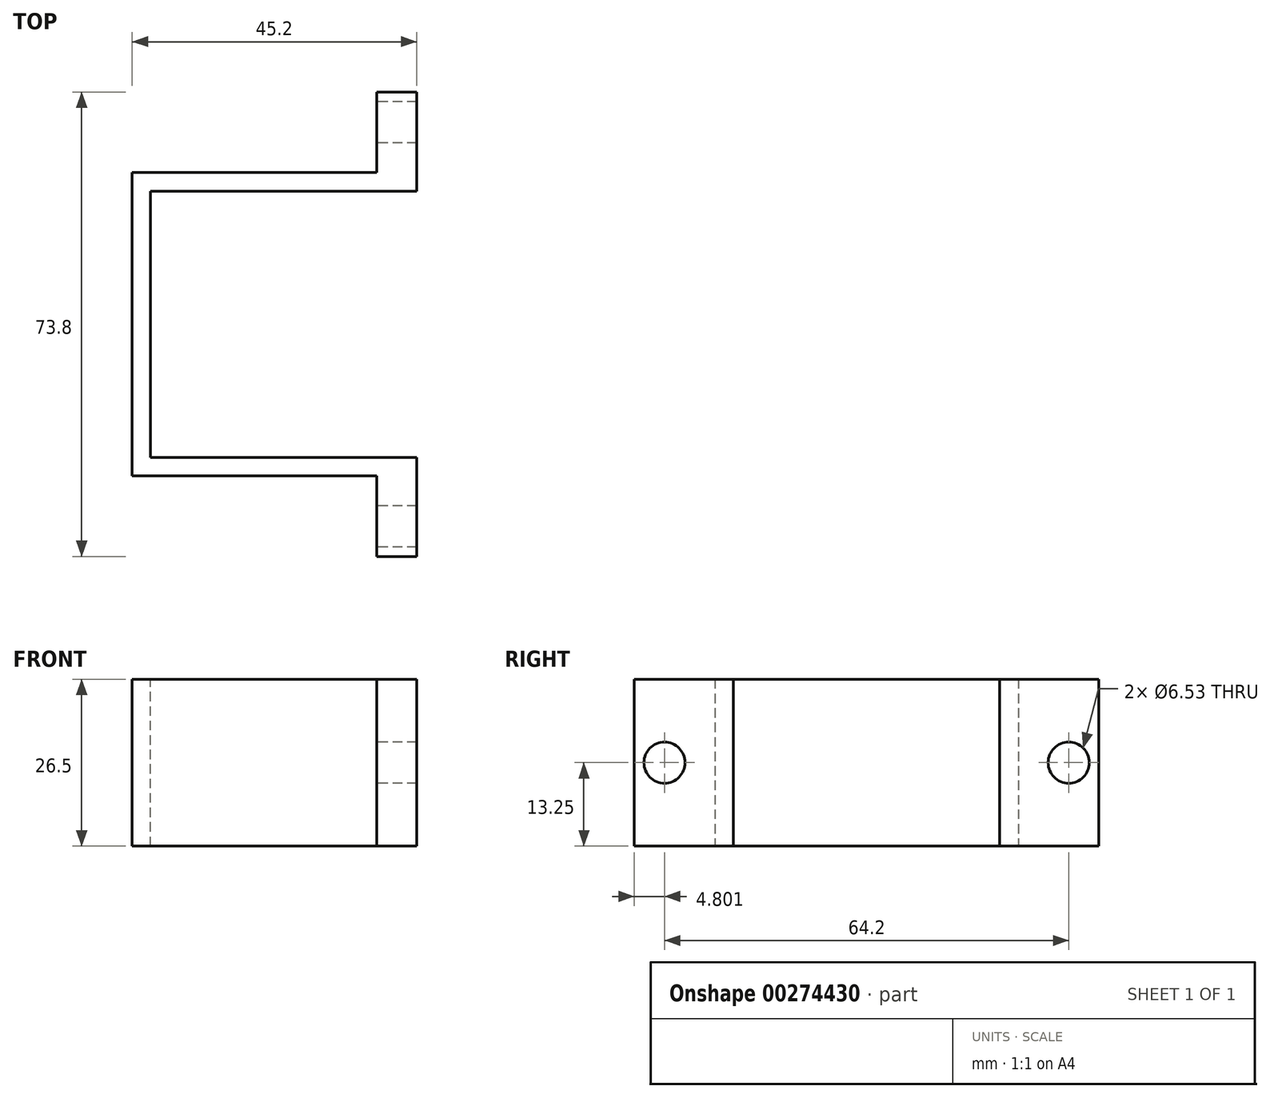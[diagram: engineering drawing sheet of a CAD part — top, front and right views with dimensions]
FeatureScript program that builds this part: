
annotation { "Feature Type Name" : "Feature", "Feature Type Description" : "" }
export const myFeature = defineFeature(function(context is Context, id is Id, definition is map)
    precondition{}
    {
        {
            var Q0;
            Q0=qCreatedBy(makeId("Top.planeOp"),FACE);
            var sketch = newSketch(context, id + "F0", { "sketchPlane" : qUnion([Q0])});
            skLineSegment(sketch, "E0.bottom", {"start": v(-33.6, 36.05) * mm, "end": v(11.6, 36.05) * mm});
            skLineSegment(sketch, "E0.top", {"start": v(-33.6, -12.15) * mm, "end": v(11.6, -12.15) * mm});
            skLineSegment(sketch, "E0.left", {"start": v(-33.6, 36.05) * mm, "end": v(-33.6, -12.15) * mm});
            skLineSegment(sketch, "E0.right", {"start": v(11.6, 36.05) * mm, "end": v(11.6, -12.15) * mm});
            skLineSegment(sketch, "E1.bottom", {"start": v(11.6, 36.05) * mm, "end": v(5.25, 36.05) * mm});
            skLineSegment(sketch, "E1.top", {"start": v(11.6, 48.85) * mm, "end": v(5.25, 48.85) * mm});
            skLineSegment(sketch, "E1.left", {"start": v(11.6, 36.05) * mm, "end": v(11.6, 48.85) * mm});
            skLineSegment(sketch, "E1.right", {"start": v(5.25, 36.05) * mm, "end": v(5.25, 48.85) * mm});
            skPoint(sketch, "E2.oppositeSnap0", {"position": v(5.25, 42.45) * mm});
            skLineSegment(sketch, "E2.bottom", {"start": v(11.6, -12.15) * mm, "end": v(5.25, -12.15) * mm});
            skLineSegment(sketch, "E2.top", {"start": v(11.6, -24.95) * mm, "end": v(5.25, -24.95) * mm});
            skLineSegment(sketch, "E2.left", {"start": v(11.6, -12.15) * mm, "end": v(11.6, -24.95) * mm});
            skLineSegment(sketch, "E2.right", {"start": v(5.25, -12.15) * mm, "end": v(5.25, -24.95) * mm});
            skSolve(sketch);
        }
        {
            var Q0;
            Q0 = qSketchRegion(id + "F0", true);
            extrude(context, id + "F1", {"entities" : qUnion([Q0]), "depth" : 26.5 * mm});
        }
        {
            var Q0;
            Q0=makeQuery(id+"F1.opExtrude","SWEPT_FACE",FACE,{"disambiguationData":[OSD([sQuery(id+"F0.wireOp",EDGE,"E2.right")])]});
            var sketch = newSketch(context, id + "F2", { "sketchPlane" : qUnion([Q0])});
            skPoint(sketch, "E3", {"position": v(20.15, 13.25) * mm});
            skPoint(sketch, "E4", {"position": v(-44.05, 13.25) * mm});
            skSolve(sketch);
        }
        {
            var Q0;
            Q0=sQuery(id+"F2.wireOp",VERTEX,"E4");
            var Q1;
            Q1=sQuery(id+"F2.wireOp",VERTEX,"E3");
            var Q2;
            Q2=makeQuery(id+"F1.opExtrude","SWEPT_BODY",BODY,{"disambiguationData":[OSD([sQuery(id+"F0.wireOp",EDGE,"E0.bottom"),sQuery(id+"F0.wireOp",EDGE,"E0.top"),sQuery(id+"F0.wireOp",EDGE,"E0.left"),sQuery(id+"F0.wireOp",EDGE,"E0.right"),sQuery(id+"F0.wireOp",EDGE,"E1.top"),sQuery(id+"F0.wireOp",EDGE,"E1.left"),sQuery(id+"F0.wireOp",EDGE,"E1.right"),sQuery(id+"F0.wireOp",EDGE,"E2.top"),sQuery(id+"F0.wireOp",EDGE,"E2.left"),sQuery(id+"F0.wireOp",EDGE,"E2.right")])]});
            hole(context, id + "F3", {"style" : HoleStyle.SIMPLE, "endStyle" : HoleEndStyle.THROUGH, "holeDiameter" : 6.53 * mm, "tappedDepth" : 12 * mm, "tapClearance" : 3, "locations" : qUnion([Q0, Q1]), "scope" : qUnion([Q2])});
        }
        {
            var Q0;
            Q0=makeQuery(id+"F1.opExtrude","CAP_FACE",FACE,{"disambiguationData":[OSD([sQuery(id+"F0.wireOp",EDGE,"E0.bottom"),sQuery(id+"F0.wireOp",EDGE,"E0.top"),sQuery(id+"F0.wireOp",EDGE,"E0.left"),sQuery(id+"F0.wireOp",EDGE,"E0.right"),sQuery(id+"F0.wireOp",EDGE,"E1.top"),sQuery(id+"F0.wireOp",EDGE,"E1.left"),sQuery(id+"F0.wireOp",EDGE,"E1.right"),sQuery(id+"F0.wireOp",EDGE,"E2.top"),sQuery(id+"F0.wireOp",EDGE,"E2.left"),sQuery(id+"F0.wireOp",EDGE,"E2.right")])],"isStart":false});
            var sketch = newSketch(context, id + "F4", { "sketchPlane" : qUnion([Q0])});
            skLineSegment(sketch, "E5.bottom", {"start": v(11.6, 33.1) * mm, "end": v(-30.7, 33.1) * mm});
            skLineSegment(sketch, "E5.top", {"start": v(11.6, -9.2) * mm, "end": v(-30.7, -9.2) * mm});
            skLineSegment(sketch, "E5.left", {"start": v(11.6, 33.1) * mm, "end": v(11.6, -9.2) * mm});
            skLineSegment(sketch, "E5.right", {"start": v(-30.7, 33.1) * mm, "end": v(-30.7, -9.2) * mm});
            skSolve(sketch);
        }
        {
            var Q0;
            Q0=makeQuery(id+"F4.imprint","IMPRINT",FACE,{"disambiguationData":[TD([[makeQuery(id+"F4.imprint","IMPRINT",EDGE,{"derivedFrom":sQuery(id+"F4.wireOp",EDGE,"E5.bottom")}),1.0]])]});
            extrude(context, id + "F5", {"entities" : qUnion([Q0]), "operationType" : NewBodyOperationType.REMOVE, "endBound" : BoundingType.UP_TO_NEXT, "oppositeDirection" : true, "depth" : 25 * mm});
        }
    });
